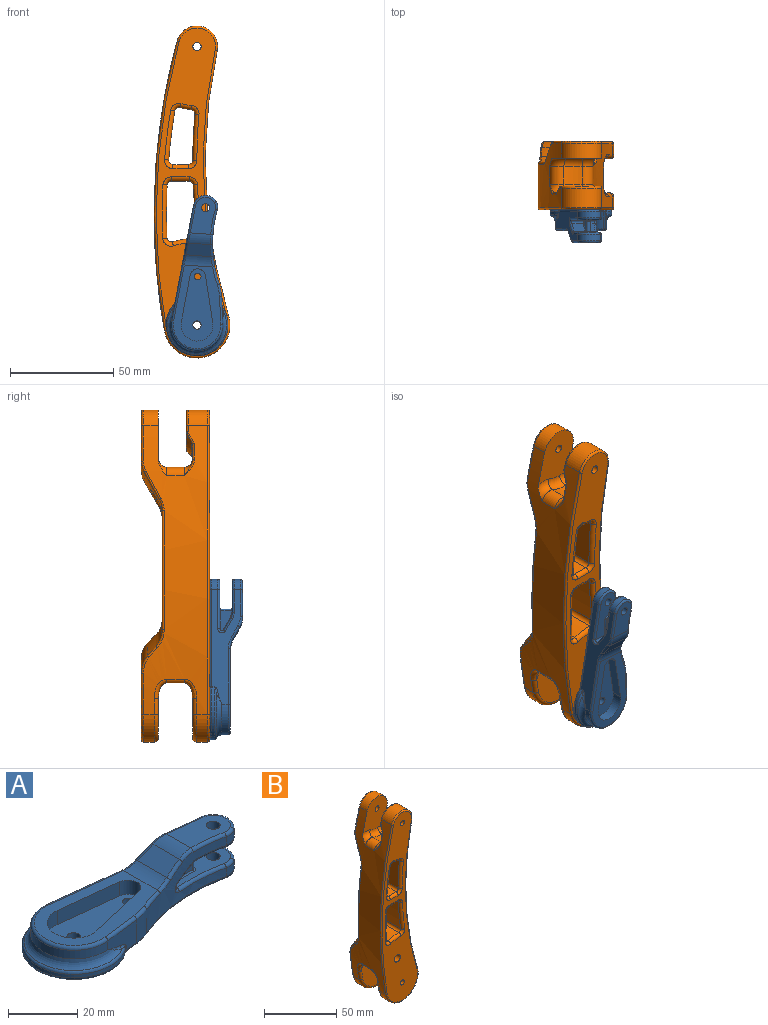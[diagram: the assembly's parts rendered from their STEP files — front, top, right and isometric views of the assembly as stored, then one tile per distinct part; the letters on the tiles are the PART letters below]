
ASSEMBLY  parts=2 mates=1
PART A: 94 faces, bbox 80.3x33.6x16 mm
  f0: plane 40.09x23mm, normal (0,0,1), area 367.2mm2, adj f20,f29,f30,f32,f34,f36,f90,f91
  f1: plane 6x5.79mm, normal (0.5,0,-0.87), area 37.7mm2, adj f4,f5,f53,f78
  f2: plane 23.66x11.99mm, normal (0,0,1), area 179.5mm2, adj f4,f10,f18,f44,f45,f47,f49,f70
  f3: plane 15.66x11.07mm, normal (0,0,-1), area 121.7mm2, adj f5,f15,f19,f52,f54,f56,f57,f75
  f4: cylinder r=1mm len=5.79mm, axis (0,-1,0), area 15mm2, adj f1,f2,f51,f76
  f5: cylinder r=5mm len=5.1mm, axis (0,-1,0), area 12.9mm2, adj f1,f3,f55,f80
  f6: cylinder r=12.5mm len=25mm, axis (0,0,-1), area 128.1mm2, adj f7,f12,f27,f30
  f7: plane 13.36x8mm, normal (0.11,-0.99,0), area 77.3mm2, adj f6,f23,f32,f61,f85,f86,f87
  f8: plane 76x28mm, normal (0,0,-1), area 1201.6mm2, adj f10,f14,f59,f60,f61,f62,f63,f64
  f9: cylinder r=6mm len=10.87mm, axis (0,0,-1), area 43.5mm2, adj f12,f24,f47,f64
  f10: cylinder r=2mm len=5mm, axis (0,0,1), area 62.8mm2, adj f2,f8
  f11: cylinder r=6mm len=10.87mm, axis (0,0,-1), area 43.5mm2, adj f12,f25,f39,f56
  f12: plane 56.26x14mm, normal (0.11,0.99,0), area 399.7mm2, adj f6,f9,f11,f29,f31,f33,f35,f37
  f13: plane 17.66x11.3mm, normal (0,0,1), area 148.6mm2, adj f15,f21,f37,f39,f41,f43
  f14: cylinder r=2mm len=5mm, axis (0,0,1), area 62.8mm2, adj f8,f58
  f15: cylinder r=2mm len=5mm, axis (0,0,1), area 62.8mm2, adj f3,f13
  f16: plane 6x3.46mm, normal (0.5,0,-0.87), area 14.5mm2, adj f18,f19,f48,f71
  f17: plane 11.96x5.75mm, normal (-0.5,0,0.87), area 74.6mm2, adj f20,f21,f33,f40
  f18: cylinder r=1mm len=2.34mm, axis (0,-1,0), area 6mm2, adj f2,f16,f46,f69
  f19: cylinder r=5mm len=2.5mm, axis (0,-1,0), area 5.1mm2, adj f3,f16,f50,f73
  f20: cylinder r=10mm len=13.78mm, axis (0,-1,0), area 67.4mm2, adj f0,f17,f31,f38
  f21: cylinder r=10mm len=10.6mm, axis (0,-1,0), area 53.8mm2, adj f13,f17,f35,f42
  f22: cylinder r=60mm len=36.11mm, axis (0,0,-1), area 273.4mm2, adj f23,f24,f25,f36,f38,f40,f42,f43
  f23: cylinder r=20mm len=8mm, axis (0,0,-1), area 47mm2, adj f7,f22,f34,f59
  f24: cylinder r=5mm len=3.9mm, axis (0,0,1), area 12.3mm2, adj f9,f22,f45,f62
  f25: cylinder r=5mm len=3.9mm, axis (0,0,1), area 12.3mm2, adj f11,f22,f41,f54
  f26: cylinder r=15mm len=30mm, axis (0,0,-1), area 84.4mm2, adj f28,f63,f83,f87
  f27: torus R=15.5mm, axis (0,0,-1), area 177.7mm2, adj f6,f28,f81,f85
  f28: torus R=14mm, axis (0,0,1), area 76.3mm2, adj f26,f27,f82,f86
  f29: cylinder r=1mm len=27.39mm, axis (0.99,-0.11,0), area 43.1mm2, adj f0,f12,f30,f31
  f30: torus R=11.5mm, axis (0,0,-1), area 64.2mm2, adj f0,f6,f29,f32
  f31: bspline ~8.99x3.39mm, area 8.7mm2, adj f12,f20,f29,f33
  f32: cylinder r=1mm len=13.48mm, axis (-0.99,-0.11,0), area 21.1mm2, adj f0,f7,f30,f34
  f33: cylinder r=1mm len=6.37mm, axis (0.86,-0.1,0.5), area 10.9mm2, adj f12,f17,f31,f35
  f34: torus R=19mm, axis (0,0,-1), area 9.1mm2, adj f0,f23,f32,f36
  f35: bspline ~5.11x2.21mm, area 8.1mm2, adj f12,f21,f33,f37
  f36: torus R=61mm, axis (0,0,-1), area 14.1mm2, adj f0,f22,f34,f38
  f37: cylinder r=1mm len=13.34mm, axis (0.99,-0.11,0), area 20.9mm2, adj f12,f13,f35,f39
  f38: bspline ~8.78x3.71mm, area 8.9mm2, adj f20,f22,f36,f40
  f39: torus R=5mm, axis (0,0,1), area 21.4mm2, adj f11,f13,f37,f41
  f40: bspline ~6.32x4.19mm, area 10.8mm2, adj f17,f22,f38,f42
  f41: torus R=4mm, axis (0,0,1), area 6mm2, adj f13,f25,f39,f43
  f42: bspline ~7.38x3.4mm, area 7.9mm2, adj f21,f22,f40,f43
  f43: torus R=61mm, axis (0,0,1), area 19.4mm2, adj f13,f22,f41,f42
  f44: torus R=61mm, axis (0,0,-1), area 28.8mm2, adj f2,f22,f45,f46
  f45: torus R=4mm, axis (0,0,-1), area 6mm2, adj f2,f24,f44,f47
  f46: bspline ~3.92x2.41mm, area 5.4mm2, adj f18,f22,f44,f48
  f47: torus R=5mm, axis (0,0,-1), area 21.4mm2, adj f2,f9,f45,f49
  f48: bspline ~6.39x4.33mm, area 10.6mm2, adj f16,f22,f46,f50
  f49: cylinder r=1mm len=19.34mm, axis (0.99,-0.11,0), area 30.4mm2, adj f2,f12,f47,f51
  f50: bspline ~5.34x2.33mm, area 4.4mm2, adj f19,f22,f48,f52
  f51: bspline ~3.74x2mm, area 5.4mm2, adj f4,f12,f49,f53
  f52: torus R=61mm, axis (0,0,1), area 16.3mm2, adj f3,f22,f50,f54
  f53: cylinder r=1mm len=6.39mm, axis (-0.86,0.1,-0.5), area 10.5mm2, adj f1,f12,f51,f55
  f54: torus R=4mm, axis (0,0,1), area 6mm2, adj f3,f25,f52,f56
  f55: bspline ~4.9x2.17mm, area 4.4mm2, adj f5,f12,f53,f57
  f56: torus R=5mm, axis (0,0,1), area 21.4mm2, adj f3,f11,f54,f57
  f57: cylinder r=1mm len=11.34mm, axis (-0.99,0.11,0), area 17.8mm2, adj f3,f12,f55,f56
  f58: plane 34.96x15.5mm, normal (0,0,1), area 370mm2, adj f14,f89,f90,f91,f92,f93
  f59: torus R=19mm, axis (0,0,1), area 9.1mm2, adj f8,f23,f60,f61
  f60: torus R=61mm, axis (0,0,1), area 58.3mm2, adj f8,f22,f59,f62
  f61: cylinder r=1mm len=5.54mm, axis (0.99,0.11,0), area 8.1mm2, adj f7,f8,f59,f88
  f62: torus R=4mm, axis (0,0,1), area 6mm2, adj f8,f24,f60,f64
  f63: torus R=14mm, axis (0,0,1), area 104.5mm2, adj f8,f26,f84,f88
  f64: torus R=5mm, axis (0,0,1), area 21.4mm2, adj f8,f9,f62,f65
  f65: cylinder r=1mm len=48.44mm, axis (-0.99,0.11,0), area 75.9mm2, adj f8,f12,f64,f84
  f66: plane 9.77x5mm, normal (0,-1,0), area 33.3mm2, adj f68,f69,f70,f71,f73,f75
  f67: plane 9.77x5mm, normal (0,1,0), area 33.3mm2, adj f68,f74,f76,f78,f79,f80
  f68: cylinder r=1mm len=5mm, axis (0,0,-1), area 15.7mm2, adj f66,f67,f72,f77
  f69: torus R=0.5mm, axis (0,-1,0), area 1.7mm2, adj f18,f66,f70,f71
  f70: cylinder r=0.5mm len=9.27mm, axis (-1,0,0), area 7.3mm2, adj f2,f66,f69,f72
  f71: cylinder r=0.5mm len=6.25mm, axis (0.87,0,0.5), area 5.4mm2, adj f16,f66,f69,f73
  f72: torus R=1.5mm, axis (0,0,-1), area 2.9mm2, adj f2,f68,f70,f74
  f73: torus R=4.5mm, axis (0,-1,0), area 2mm2, adj f19,f66,f71,f75
  f74: cylinder r=0.5mm len=9.27mm, axis (1,0,0), area 7.3mm2, adj f2,f67,f72,f76
  f75: cylinder r=0.5mm len=1.27mm, axis (1,0,0), area 1mm2, adj f3,f66,f73,f77
  f76: torus R=0.5mm, axis (0,-1,0), area 1.7mm2, adj f4,f67,f74,f78
  f77: torus R=1.5mm, axis (0,0,1), area 2.9mm2, adj f3,f68,f75,f79
  f78: cylinder r=0.5mm len=6.25mm, axis (-0.87,0,-0.5), area 5.4mm2, adj f1,f67,f76,f80
  f79: cylinder r=0.5mm len=1.27mm, axis (-1,0,0), area 1mm2, adj f3,f67,f77,f80
  f80: torus R=4.5mm, axis (0,-1,0), area 2mm2, adj f5,f67,f78,f79
  f81: bspline ~6.78x2.95mm, area 2.6mm2, adj f12,f27,f82
  f82: bspline ~4x2.05mm, area 2.6mm2, adj f12,f28,f81,f83
  f83: cylinder r=1mm len=1.25mm, axis (0,0,-1), area 0.7mm2, adj f12,f26,f82,f84
  f84: bspline ~1.2x1.14mm, area 0.4mm2, adj f63,f65,f83
  f85: bspline ~5.9x2.78mm, area 2.6mm2, adj f7,f27,f86
  f86: bspline ~3.05x2.16mm, area 2.6mm2, adj f7,f28,f85,f87
  f87: cylinder r=1mm len=1.25mm, axis (0,0,-1), area 0.7mm2, adj f7,f26,f86,f88
  f88: bspline ~1.2x1.14mm, area 0.4mm2, adj f61,f63,f87
  f89: cylinder r=1.6mm len=5mm, axis (0,0,1), area 50.3mm2, adj f8,f58
  f90: plane 22.55x5.25mm, normal (-0.23,0.97,0), area 115.8mm2, adj f0,f58,f91,f93
  f91: cylinder r=3.75mm len=7.38mm, axis (0,0,-1), area 52.5mm2, adj f0,f58,f90,f92
  f92: plane 23.01x5mm, normal (-0.11,-0.99,0), area 115.8mm2, adj f0,f58,f91,f93
  f93: cylinder r=7.75mm len=15.5mm, axis (0,0,-1), area 135mm2, adj f0,f58,f90,f92
PART B: 154 faces, bbox 64.5x34.1x163.1 mm
  f0: cylinder r=1.6mm len=4mm, axis (0,1,0), area 40.2mm2, adj f128,f153
  f1: plane 39.86x32.72mm, normal (0,1,0), area 645.9mm2, adj f29,f111,f113,f115,f148,f149,f150,f151
  f2: plane 19.55x10.12mm, normal (0,1,0), area 64.2mm2, adj f35,f36,f37,f132,f138,f145
  f3: cylinder r=2mm len=4mm, axis (0,-1,0), area 40.8mm2, adj f16,f128
  f4: plane 159x34.81mm, normal (0,-1,0), area 2569.5mm2, adj f20,f21,f88,f89,f90,f91,f92,f93
  f5: torus R=42.39mm, axis (0,1,0), area 15.8mm2, adj f23,f25,f72,f122
  f6: plane 28.72x21.86mm, normal (0,1,0), area 464.9mm2, adj f22,f26,f112,f114,f116
  f7: cylinder r=250mm len=128.09mm, axis (0,1,0), area 2624mm2, adj f9,f10,f11,f12,f14,f31,f32,f40
  f8: cylinder r=320mm len=140.45mm, axis (0,1,0), area 2865.1mm2, adj f9,f10,f11,f12,f14,f30,f34,f39
  f9: cylinder r=10mm len=19.65mm, axis (0,1,0), area 224.2mm2, adj f7,f8,f14,f114
  f10: cylinder r=16mm len=31.75mm, axis (0,1,0), area 274.3mm2, adj f7,f8,f49,f113
  f11: cylinder r=10mm len=19.65mm, axis (0,1,0), area 286.1mm2, adj f7,f8,f125,f135
  f12: cylinder r=16mm len=31.75mm, axis (0,1,0), area 274.3mm2, adj f7,f8,f38,f126
  f13: cylinder r=20mm len=8.93mm, axis (0,-1,0), area 78.1mm2, adj f30,f31,f33,f36
  f14: plane 28.25x23.78mm, normal (0,-1,0), area 465.9mm2, adj f7,f8,f9,f22,f32,f33,f34
  f15: cylinder r=20mm len=23.05mm, axis (0,-1,0), area 214.2mm2, adj f18,f19,f43,f44
  f16: plane 30x29.09mm, normal (0,-1,0), area 672.8mm2, adj f3,f19,f47,f48,f49
  f17: plane 30x29.09mm, normal (0,1,0), area 672.8mm2, adj f18,f20,f38,f39,f40
  f18: torus R=16mm, axis (0,-1,0), area 188.8mm2, adj f15,f17,f41,f42
  f19: torus R=16mm, axis (0,-1,0), area 369.2mm2, adj f15,f16,f45,f46
  f20: cylinder r=2mm len=8.25mm, axis (0,-1,0), area 103.7mm2, adj f4,f17
  f21: cylinder r=2mm len=11.25mm, axis (0,-1,0), area 141.4mm2, adj f4,f129
  f22: cylinder r=2mm len=8.25mm, axis (0,-1,0), area 103.7mm2, adj f6,f14
  f23: plane 57.65x25.4mm, normal (0,1,0), area 398mm2, adj f5,f27,f28,f66,f67,f68,f69,f70
  f24: cone r=29mm half-angle=45deg, axis (0,-1,0), area 163.7mm2, adj f28,f29,f107,f119
  f25: cone r=39.72mm half-angle=60deg, axis (0,-1,0), area 190.1mm2, adj f5,f26,f27,f73,f74,f75,f76,f77
  f26: torus R=19.72mm, axis (0,-1,0), area 105.7mm2, adj f6,f25,f110,f118
  f27: torus R=42.39mm, axis (0,1,0), area 16.1mm2, adj f23,f25,f71,f106
  f28: torus R=43.14mm, axis (0,1,0), area 172.4mm2, adj f23,f24,f82,f84,f86,f105,f121
  f29: torus R=24.86mm, axis (0,-1,0), area 215.9mm2, adj f1,f24,f109,f117,f149
  f30: cylinder r=5mm len=8.5mm, axis (0,1,0), area 77mm2, adj f8,f13,f34,f37
  f31: cylinder r=5mm len=8.5mm, axis (0,-1,0), area 73.3mm2, adj f7,f13,f32,f35
  f32: torus R=9mm, axis (0,-1,0), area 48.2mm2, adj f7,f14,f31,f33
  f33: torus R=16mm, axis (0,-1,0), area 53.5mm2, adj f13,f14,f32,f34
  f34: torus R=9mm, axis (0,-1,0), area 51.1mm2, adj f8,f14,f30,f33
  f35: torus R=9mm, axis (0,-1,0), area 45.3mm2, adj f2,f31,f36,f139
  f36: torus R=16mm, axis (0,-1,0), area 53.5mm2, adj f2,f13,f35,f37
  f37: torus R=9mm, axis (0,-1,0), area 48.2mm2, adj f2,f30,f36,f131
  f38: torus R=14mm, axis (0,-1,0), area 156.7mm2, adj f12,f17,f39,f40
  f39: torus R=318mm, axis (0,-1,0), area 25mm2, adj f8,f17,f38,f41
  f40: torus R=252mm, axis (0,-1,0), area 23.6mm2, adj f7,f17,f38,f42
  f41: bspline ~12.52x7.08mm, area 40.3mm2, adj f8,f18,f39,f43
  f42: bspline ~9.85x7.11mm, area 38.2mm2, adj f7,f18,f40,f44
  f43: cylinder r=2mm len=8.5mm, axis (0,1,0), area 38.9mm2, adj f8,f15,f41,f45
  f44: cylinder r=2mm len=8.5mm, axis (0,-1,0), area 37.9mm2, adj f7,f15,f42,f46
  f45: bspline ~12.52x7.08mm, area 40.3mm2, adj f8,f19,f43,f47
  f46: bspline ~9.85x7.11mm, area 38.2mm2, adj f7,f19,f44,f48
  f47: torus R=318mm, axis (0,-1,0), area 25mm2, adj f8,f16,f45,f49
  f48: torus R=252mm, axis (0,-1,0), area 23.6mm2, adj f7,f16,f46,f49
  f49: torus R=14mm, axis (0,-1,0), area 156.7mm2, adj f10,f16,f47,f48
  f50: cylinder r=42.07mm len=19.4mm, axis (0,-1,0), area 205.8mm2, adj f63,f64,f84,f92
  f51: plane 19x8.69mm, normal (0,0,-1), area 165mm2, adj f62,f65,f81,f91
  f52: cylinder r=314mm len=25.75mm, axis (0,-1,0), area 489.3mm2, adj f62,f63,f85,f95
  f53: cylinder r=256mm len=23.59mm, axis (0,-1,0), area 450.2mm2, adj f64,f65,f78,f88
  f54: cylinder r=30.72mm len=25.04mm, axis (0,-1,0), area 139.4mm2, adj f59,f60,f77,f99
  f55: plane 19x7.67mm, normal (0,0,1), area 145.7mm2, adj f58,f61,f66,f100
  f56: cylinder r=256mm len=22.6mm, axis (0,-1,0), area 440.8mm2, adj f58,f59,f70,f72,f74,f96
  f57: cylinder r=314mm len=23.84mm, axis (0,-1,0), area 468.8mm2, adj f60,f61,f69,f71,f73,f103
  f58: cylinder r=2mm len=19mm, axis (0,-1,0), area 59.6mm2, adj f55,f56,f68,f98
  f59: cylinder r=2mm len=25.04mm, axis (0,1,0), area 74.7mm2, adj f54,f56,f76,f97
  f60: cylinder r=2mm len=25.04mm, axis (0,-1,0), area 79.8mm2, adj f54,f57,f75,f101
  f61: cylinder r=2mm len=19mm, axis (0,-1,0), area 62.9mm2, adj f55,f57,f67,f102
  f62: cylinder r=2mm len=19mm, axis (0,-1,0), area 58mm2, adj f51,f52,f83,f93
  f63: cylinder r=2mm len=19.4mm, axis (0,-1,0), area 69.8mm2, adj f50,f52,f86,f87,f94
  f64: cylinder r=2mm len=19.4mm, axis (0,1,0), area 64mm2, adj f50,f53,f80,f82,f90
  f65: cylinder r=2mm len=19mm, axis (0,-1,0), area 58mm2, adj f51,f53,f79,f89
  f66: cylinder r=2mm len=7.67mm, axis (1,0,0), area 24.1mm2, adj f23,f55,f67,f68
  f67: torus R=4mm, axis (0,1,0), area 14.2mm2, adj f23,f61,f66,f69
  f68: torus R=4mm, axis (0,1,0), area 13.4mm2, adj f23,f58,f66,f70
  f69: torus R=316mm, axis (0,1,0), area 46.8mm2, adj f23,f57,f67,f71
  f70: torus R=254mm, axis (0,1,0), area 40.4mm2, adj f23,f56,f68,f72
  f71: bspline ~8.56x4.2mm, area 18.6mm2, adj f27,f57,f69,f73
  f72: bspline ~8.56x4.06mm, area 18mm2, adj f5,f56,f70,f74
  f73: bspline ~16.14x10.61mm, area 11.8mm2, adj f25,f57,f71,f75
  f74: bspline ~13.31x8.85mm, area 13mm2, adj f25,f56,f72,f76
  f75: bspline ~5.96x4.97mm, area 14.7mm2, adj f25,f60,f73,f77
  f76: bspline ~5.35x4.74mm, area 13.3mm2, adj f25,f59,f74,f77
  f77: torus R=28.72mm, axis (0,1,0), area 11.5mm2, adj f25,f54,f75,f76
  f78: torus R=254mm, axis (0,1,0), area 74.2mm2, adj f23,f53,f79,f80
  f79: torus R=4mm, axis (0,1,0), area 13.1mm2, adj f23,f65,f78,f81
  f80: torus R=4mm, axis (0,1,0), area 3.2mm2, adj f23,f64,f78,f82
  f81: cylinder r=2mm len=8.69mm, axis (-1,0,0), area 27.3mm2, adj f23,f51,f79,f83
  f82: bspline ~4.75x3.44mm, area 9.7mm2, adj f28,f64,f80,f84
  f83: torus R=4mm, axis (0,1,0), area 13.1mm2, adj f23,f62,f81,f85
  f84: torus R=40.07mm, axis (0,-1,0), area 27.5mm2, adj f28,f50,f82,f86
  f85: torus R=316mm, axis (0,1,0), area 81.1mm2, adj f23,f52,f83,f87
  f86: bspline ~5.53x2.86mm, area 9.7mm2, adj f28,f63,f84,f87
  f87: torus R=4mm, axis (0,1,0), area 4.6mm2, adj f23,f63,f85,f86
  f88: torus R=254mm, axis (0,-1,0), area 74.2mm2, adj f4,f53,f89,f90
  f89: torus R=4mm, axis (0,-1,0), area 13.1mm2, adj f4,f65,f88,f91
  f90: torus R=4mm, axis (0,-1,0), area 14.3mm2, adj f4,f64,f88,f92
  f91: cylinder r=2mm len=8.69mm, axis (1,0,0), area 27.3mm2, adj f4,f51,f89,f93
  f92: torus R=40.07mm, axis (0,-1,0), area 32.8mm2, adj f4,f50,f90,f94
  f93: torus R=4mm, axis (0,-1,0), area 13.1mm2, adj f4,f62,f91,f95
  f94: torus R=4mm, axis (0,-1,0), area 15.6mm2, adj f4,f63,f92,f95
  f95: torus R=316mm, axis (0,-1,0), area 81.1mm2, adj f4,f52,f93,f94
  f96: torus R=254mm, axis (0,-1,0), area 70.4mm2, adj f4,f56,f97,f98
  f97: torus R=4mm, axis (0,-1,0), area 13.4mm2, adj f4,f59,f96,f99
  f98: torus R=4mm, axis (0,-1,0), area 13.4mm2, adj f4,f58,f96,f100
  f99: torus R=28.72mm, axis (0,-1,0), area 17.1mm2, adj f4,f54,f97,f101
  f100: cylinder r=2mm len=7.67mm, axis (-1,0,0), area 24.1mm2, adj f4,f55,f98,f102
  f101: torus R=4mm, axis (0,-1,0), area 14.4mm2, adj f4,f60,f99,f103
  f102: torus R=4mm, axis (0,-1,0), area 14.2mm2, adj f4,f61,f100,f103
  f103: torus R=316mm, axis (0,-1,0), area 75.6mm2, adj f4,f57,f101,f102
  f104: torus R=319mm, axis (0,1,0), area 90.9mm2, adj f8,f23,f105,f106
  f105: bspline ~10.98x4.71mm, area 12.6mm2, adj f8,f28,f104,f107
  f106: bspline ~7.32x2.48mm, area 8.5mm2, adj f8,f27,f104,f108
  f107: bspline ~15x13.11mm, area 7.7mm2, adj f8,f24,f105,f109
  f108: bspline ~29.72x16.87mm, area 21.5mm2, adj f8,f25,f106,f110
  f109: bspline ~11.86x5.08mm, area 12mm2, adj f8,f29,f107,f111
  f110: bspline ~9.03x3.38mm, area 8.1mm2, adj f8,f26,f108,f112
  f111: torus R=319mm, axis (0,-1,0), area 32mm2, adj f1,f8,f109,f113
  f112: torus R=319mm, axis (0,-1,0), area 28mm2, adj f6,f8,f110,f114
  f113: torus R=15mm, axis (0,-1,0), area 80.2mm2, adj f1,f10,f111,f115
  f114: torus R=9mm, axis (0,-1,0), area 46.8mm2, adj f6,f9,f112,f116
  f115: torus R=251mm, axis (0,-1,0), area 30.2mm2, adj f1,f7,f113,f117
  f116: torus R=251mm, axis (0,-1,0), area 27mm2, adj f6,f7,f114,f118
  f117: bspline ~9.88x4mm, area 11.7mm2, adj f7,f29,f115,f119
  f118: bspline ~8.82x3.38mm, area 7.9mm2, adj f7,f26,f116,f120
  f119: bspline ~13.84x13.12mm, area 7.9mm2, adj f7,f24,f117,f121
  f120: bspline ~28.66x16.82mm, area 21.7mm2, adj f7,f25,f118,f122
  f121: bspline ~9.24x4.74mm, area 12.4mm2, adj f7,f28,f119,f123
  f122: bspline ~7.83x2.96mm, area 8.4mm2, adj f5,f7,f120,f123
  f123: torus R=251mm, axis (0,1,0), area 78.5mm2, adj f7,f23,f121,f122
  f124: torus R=319mm, axis (0,-1,0), area 222.4mm2, adj f4,f8,f125,f126
  f125: torus R=9mm, axis (0,-1,0), area 46.8mm2, adj f4,f11,f124,f127
  f126: torus R=15mm, axis (0,-1,0), area 80.2mm2, adj f4,f12,f124,f127
  f127: torus R=251mm, axis (0,-1,0), area 204mm2, adj f4,f7,f125,f126
  f128: plane 34.64x16.54mm, normal (0,1,0), area 375.1mm2, adj f0,f3,f148,f149,f150,f151
  f129: plane 18.59x18.55mm, normal (0,1,0), area 256.7mm2, adj f21,f134,f135,f136,f141
  f130: cone r=10mm half-angle=45deg, axis (0,-1,0), area 84mm2, adj f133,f137,f141,f144,f145,f146
  f131: bspline ~7.98x5mm, area 5.4mm2, adj f8,f37,f132
  f132: torus R=319mm, axis (0,-1,0), area 11.8mm2, adj f2,f8,f131,f146,f147
  f133: bspline ~9.26x5.08mm, area 5.8mm2, adj f8,f130,f140,f147
  f134: torus R=319mm, axis (0,1,0), area 5.3mm2, adj f8,f129,f135,f140
  f135: torus R=9mm, axis (0,1,0), area 46.8mm2, adj f11,f129,f134,f136
  f136: torus R=251mm, axis (0,1,0), area 5.1mm2, adj f7,f129,f135,f142
  f137: bspline ~7.2x4.58mm, area 5.7mm2, adj f7,f130,f142,f143
  f138: torus R=251mm, axis (0,-1,0), area 10.6mm2, adj f2,f7,f139,f143,f144
  f139: bspline ~8.04x5mm, area 5.3mm2, adj f7,f35,f138
  f140: sphere r=1mm, area 0.1mm2, adj f133,f134,f141
  f141: torus R=9.59mm, axis (0,1,0), area 19.5mm2, adj f129,f130,f140,f142
  f142: sphere r=1mm, area 0.2mm2, adj f136,f137,f141
  f143: bspline ~1.12x0.78mm, area 0.2mm2, adj f137,f138,f144
  f144: bspline ~1.8x1.39mm, area 0.6mm2, adj f130,f138,f143,f145
  f145: torus R=13.41mm, axis (0,-1,0), area 15.6mm2, adj f2,f130,f144,f146
  f146: bspline ~1.34x1.09mm, area 0.6mm2, adj f130,f132,f145,f147
  f147: bspline ~1.11x0.72mm, area 0.2mm2, adj f132,f133,f146
  f148: plane 23.16x5mm, normal (1,0,0.04), area 115.9mm2, adj f1,f128,f149,f151
  f149: cylinder r=3.9mm len=7.53mm, axis (0,1,0), area 53.1mm2, adj f1,f29,f128,f148,f150
  f150: plane 21.58x8.47mm, normal (-0.93,0,-0.37), area 115.9mm2, adj f1,f128,f149,f151
  f151: cylinder r=7.75mm len=15.49mm, axis (0,1,0), area 134.5mm2, adj f1,f128,f148,f150
  f152: cylinder r=3mm len=22.6mm, axis (0,-1,0), area 426mm2, adj f4,f153
  f153: cone r=1.6mm half-angle=45deg, axis (0,-1,0), area 28.6mm2, adj f0,f152
PLACE A rot(axis=(0.61,-0.56,0.56),117.6deg) t=(103.31,76.57,-24.1)mm
PLACE B t=(103.31,93.07,-24.1)mm fixed
MATE revolute A.f6 <-> B.f3  axis (0,1,0) through (103.31,76.57,-24.1)mm
